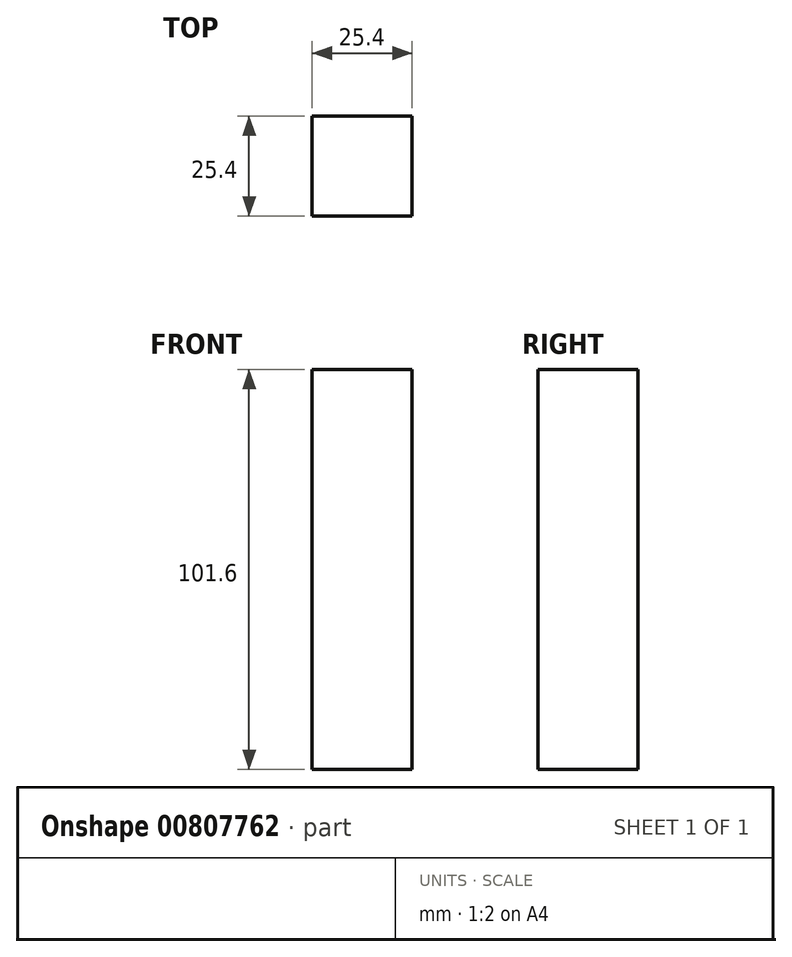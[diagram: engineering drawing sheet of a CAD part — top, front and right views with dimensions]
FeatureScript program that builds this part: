
annotation { "Feature Type Name" : "Feature", "Feature Type Description" : "" }
export const myFeature = defineFeature(function(context is Context, id is Id, definition is map)
    precondition{}
    {
        {
            var Q0;
            Q0=qCreatedBy(makeId("Right.planeOp"),FACE);
            var sketch = newSketch(context, id + "F0", { "sketchPlane" : qUnion([Q0])});
            skLineSegment(sketch, "E0.bottom", {"start": v(12.7, 31.53) * mm, "end": v(-12.7, 31.53) * mm});
            skLineSegment(sketch, "E0.top", {"start": v(12.7, -70.07) * mm, "end": v(-12.7, -70.07) * mm});
            skLineSegment(sketch, "E0.left", {"start": v(12.7, 31.53) * mm, "end": v(12.7, -70.07) * mm});
            skLineSegment(sketch, "E0.right", {"start": v(-12.7, 31.53) * mm, "end": v(-12.7, -70.07) * mm});
            skPoint(sketch, "E0.middle", {"position": v(0, -19.27) * mm});
            skSolve(sketch);
        }
        {
            var Q0;
            Q0=makeQuery(id+"F0.imprint","IMPRINT",FACE,{"disambiguationData":[TD([[makeQuery(id+"F0.imprint","IMPRINT",EDGE,{"derivedFrom":sQuery(id+"F0.wireOp",EDGE,"E0.bottom")}),1.0]])]});
            extrude(context, id + "F1", {"entities" : qUnion([Q0]), "depth" : 25.4 * mm, "offsetDistance" : 25.4 * mm});
        }
    });
